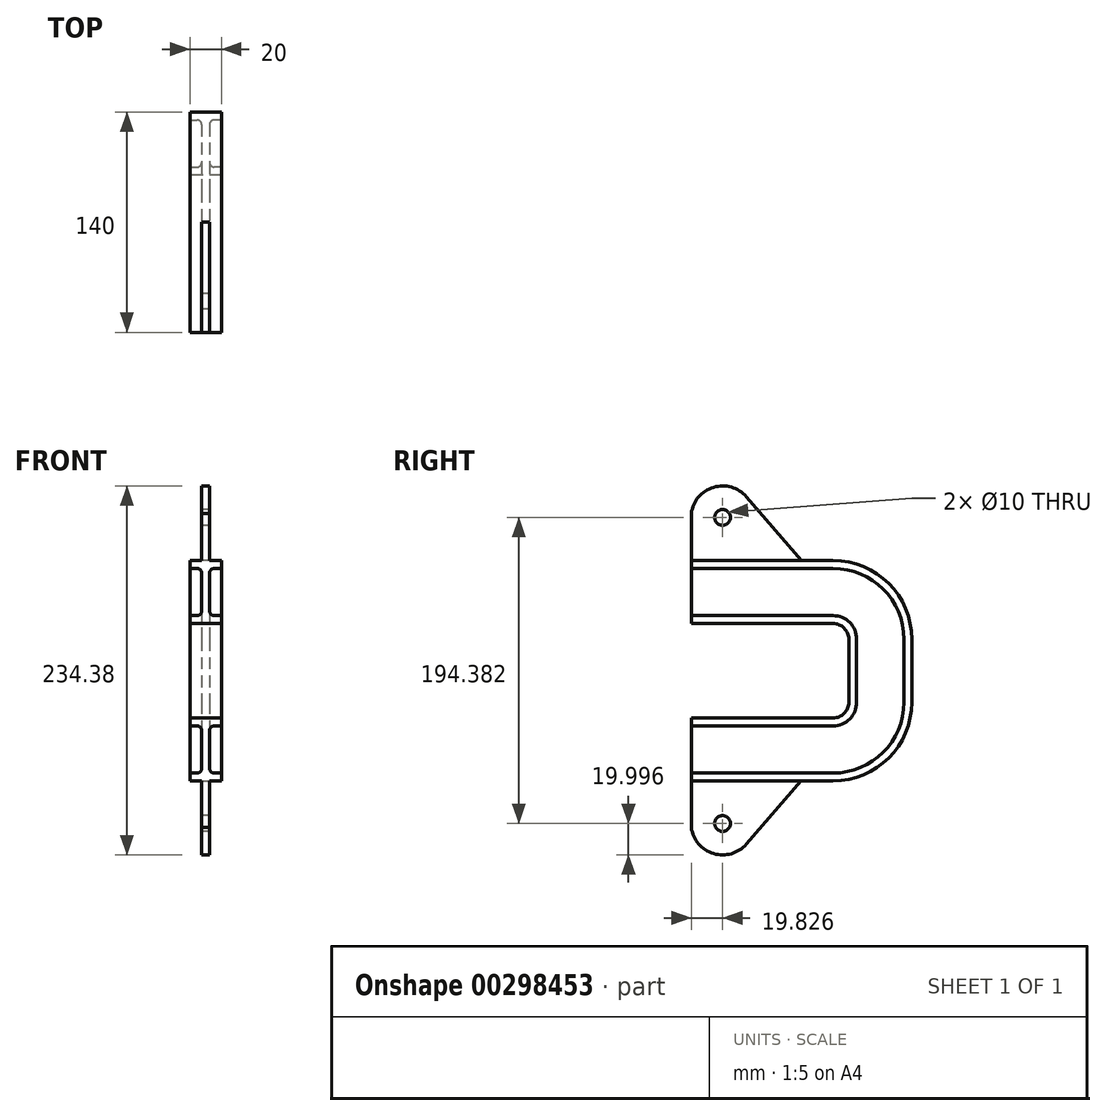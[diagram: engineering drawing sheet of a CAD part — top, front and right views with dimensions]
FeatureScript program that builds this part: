
annotation { "Feature Type Name" : "Feature", "Feature Type Description" : "" }
export const myFeature = defineFeature(function(context is Context, id is Id, definition is map)
    precondition{}
    {
        {
            var Q0;
            Q0=qCreatedBy(makeId("Front.planeOp"),FACE);
            var sketch = newSketch(context, id + "F0", { "sketchPlane" : qUnion([Q0])});
            skLineSegment(sketch, "E0", {"start": v(0, 20) * mm, "end": v(10, 20) * mm});
            skLineSegment(sketch, "E1", {"start": v(10, 20) * mm, "end": v(10, 15) * mm});
            skLineSegment(sketch, "E2", {"start": v(10, 15) * mm, "end": v(5.5, 15) * mm});
            skLineSegment(sketch, "E3", {"start": v(2.5, 12) * mm, "end": v(2.5, 0) * mm});
            skPoint(sketch, "E4.visualSharp", {"position": v(2.5, 15) * mm});
            skArc(sketch, "E4.filletArc", {"start": v(5.5, 15) * mm, "mid": v(3.38, 14.12) * mm, "end": v(2.5, 12) * mm});
            skArc(sketch, "E5.MirrorCS", {"start": v(-5.5, 15) * mm, "mid": v(-3.38, 14.12) * mm, "end": v(-2.5, 12) * mm});
            skLineSegment(sketch, "E6.MirrorCS", {"start": v(0, 20) * mm, "end": v(-10, 20) * mm});
            skLineSegment(sketch, "E7.MirrorCS", {"start": v(-10, 15) * mm, "end": v(-5.5, 15) * mm});
            skLineSegment(sketch, "E8.MirrorCS", {"start": v(-2.5, 12) * mm, "end": v(-2.5, 0) * mm});
            skLineSegment(sketch, "E9.MirrorCS", {"start": v(-10, 20) * mm, "end": v(-10, 15) * mm});
            skPoint(sketch, "E10.MirrorP", {"position": v(-2.5, 15) * mm});
            skArc(sketch, "E11.MirrorCS", {"start": v(5.5, -15) * mm, "mid": v(3.38, -14.12) * mm, "end": v(2.5, -12) * mm});
            skArc(sketch, "E12.MirrorCS", {"start": v(-5.5, -15) * mm, "mid": v(-3.38, -14.12) * mm, "end": v(-2.5, -12) * mm});
            skLineSegment(sketch, "E13.MirrorCS", {"start": v(0, -20) * mm, "end": v(-10, -20) * mm});
            skPoint(sketch, "E14.MirrorP", {"position": v(-2.5, -15) * mm});
            skLineSegment(sketch, "E15.MirrorCS", {"start": v(-2.5, -12) * mm, "end": v(-2.5, 0) * mm});
            skLineSegment(sketch, "E16.MirrorCS", {"start": v(10, -15) * mm, "end": v(5.5, -15) * mm});
            skLineSegment(sketch, "E17.MirrorCS", {"start": v(2.5, -12) * mm, "end": v(2.5, 0) * mm});
            skLineSegment(sketch, "E18.MirrorCS", {"start": v(0, -20) * mm, "end": v(10, -20) * mm});
            skLineSegment(sketch, "E19.MirrorCS", {"start": v(-10, -20) * mm, "end": v(-10, -15) * mm});
            skLineSegment(sketch, "E20.MirrorCS", {"start": v(-10, -15) * mm, "end": v(-5.5, -15) * mm});
            skPoint(sketch, "E21.MirrorP", {"position": v(2.5, -15) * mm});
            skLineSegment(sketch, "E22.MirrorCS", {"start": v(10, -20) * mm, "end": v(10, -15) * mm});
            skSolve(sketch);
        }
        {
            var Q0;
            Q0=qCreatedBy(makeId("Right.planeOp"),FACE);
            var sketch = newSketch(context, id + "F1", { "sketchPlane" : qUnion([Q0])});
            skLineSegment(sketch, "E23", {"start": v(0, -20) * mm, "end": v(90, -20) * mm});
            skLineSegment(sketch, "E24", {"start": v(100, -30) * mm, "end": v(100, -70) * mm});
            skLineSegment(sketch, "E25", {"start": v(90, -80) * mm, "end": v(0, -80) * mm});
            skPoint(sketch, "E26.visualSharp", {"position": v(100, -20) * mm});
            skArc(sketch, "E26.filletArc", {"start": v(100, -30) * mm, "mid": v(97.07, -22.93) * mm, "end": v(90, -20) * mm});
            skPoint(sketch, "E27.visualSharp", {"position": v(100, -80) * mm});
            skArc(sketch, "E27.filletArc", {"start": v(90, -80) * mm, "mid": v(97.07, -77.07) * mm, "end": v(100, -70) * mm});
            skSolve(sketch);
        }
        {
            var Q0;
            Q0 = qSketchRegion(id + "F0", true);
            var Q1;
            Q1 = qConstructionFilter(qBodyType(qCreatedBy(id + "F1" ,EDGE), BodyType.WIRE), ConstructionObject.NO);
            sweep(context, id + "F2", {"profiles" : qUnion([Q0]), "path" : qUnion([Q1])});
        }
        {
            var Q0;
            Q0=qCreatedBy(makeId("Right.planeOp"),FACE);
            var sketch = newSketch(context, id + "F3", { "sketchPlane" : qUnion([Q0])});
            skLineSegment(sketch, "E28", {"start": v(0, 20) * mm, "end": v(70, 20) * mm});
            skLineSegment(sketch, "E29", {"start": v(70, 20) * mm, "end": v(34.94, 60.46) * mm});
            skArc(sketch, "E30", {"start": v(34.94, 60.46) * mm, "mid": v(14.09, 66.53) * mm, "end": v(0, 50) * mm});
            skLineSegment(sketch, "E31", {"start": v(0, 50) * mm, "end": v(0, 20) * mm});
            skCircle(sketch, "E32", {"center": v(19.83, 47.37) * mm, "radius": 5 * mm});
            skLineSegment(sketch, "E33", {"start": v(79.33, -49.82) * mm, "end": v(179.64, -49.82) * mm, "construction": true});
            skLineSegment(sketch, "E34.MirrorCS", {"start": v(0, -119.65) * mm, "end": v(70, -119.65) * mm});
            skArc(sketch, "E35.MirrorCS", {"start": v(34.94, -160.11) * mm, "mid": v(14.09, -166.17) * mm, "end": v(0, -149.65) * mm});
            skLineSegment(sketch, "E36.MirrorCS", {"start": v(70, -119.65) * mm, "end": v(34.94, -160.11) * mm});
            skLineSegment(sketch, "E37.MirrorCS", {"start": v(0, -149.65) * mm, "end": v(0, -119.65) * mm});
            skCircle(sketch, "E38.MirrorC", {"center": v(19.83, -147.01) * mm, "radius": 5 * mm});
            skSolve(sketch);
        }
        {
            var Q0;
            Q0 = qSketchRegion(id + "F3", true);
            extrude(context, id + "F4", {"entities" : qUnion([Q0]), "operationType" : NewBodyOperationType.ADD, "endBound" : BoundingType.SYMMETRIC, "depth" : 5 * mm});
        }
    });
